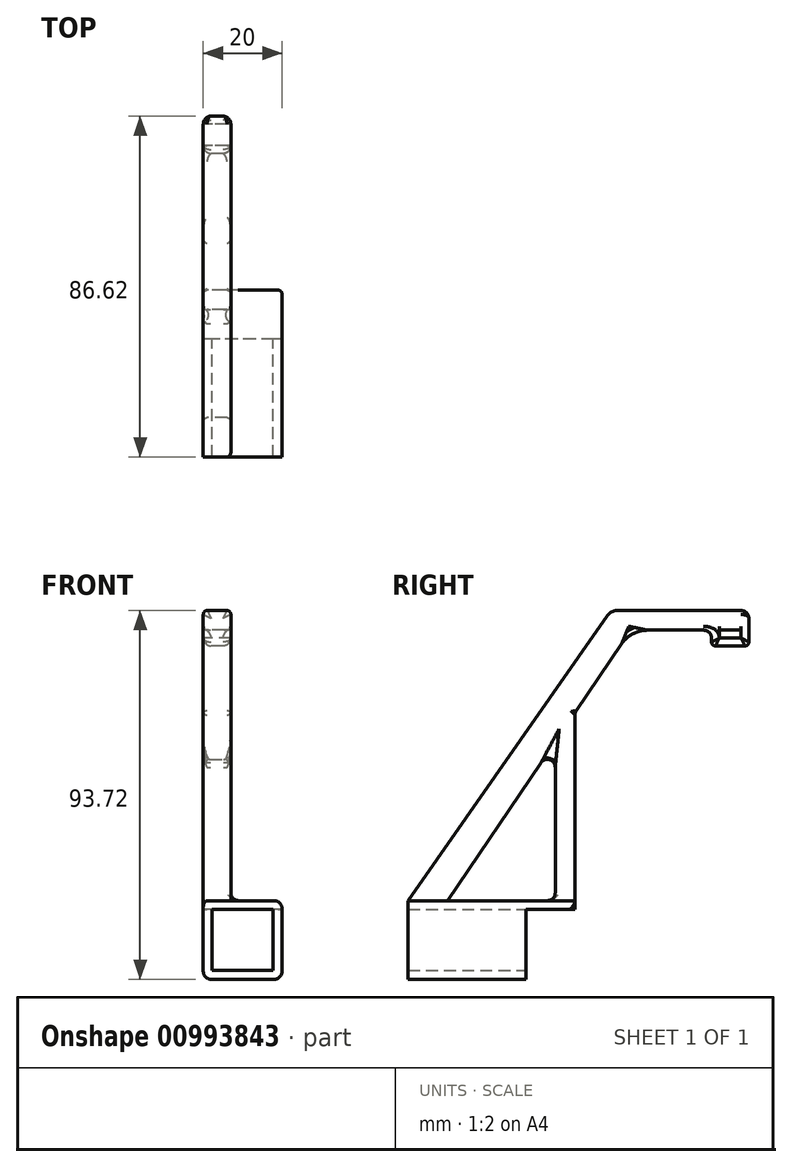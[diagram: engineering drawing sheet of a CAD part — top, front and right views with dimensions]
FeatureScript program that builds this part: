
annotation { "Feature Type Name" : "Feature", "Feature Type Description" : "" }
export const myFeature = defineFeature(function(context is Context, id is Id, definition is map)
    precondition{}
    {
        {
            var Q0;
            Q0=qCreatedBy(makeId("Right.planeOp"),FACE);
            var sketch = newSketch(context, id + "F0", { "sketchPlane" : qUnion([Q0])});
            skLineSegment(sketch, "E0.bottom", {"start": v(-15, 0) * mm, "end": v(15, 0) * mm});
            skLineSegment(sketch, "E0.top", {"start": v(-15, -20) * mm, "end": v(15, -20) * mm});
            skLineSegment(sketch, "E0.left", {"start": v(-15, 0) * mm, "end": v(-15, -20) * mm});
            skLineSegment(sketch, "E0.right", {"start": v(15, 0) * mm, "end": v(15, -20) * mm});
            skLineSegment(sketch, "E1", {"start": v(15, 0) * mm, "end": v(-36.62, 73.72) * mm});
            skLineSegment(sketch, "E2", {"start": v(-36.62, 73.72) * mm, "end": v(-71.62, 73.72) * mm});
            skLineSegment(sketch, "E3", {"start": v(-71.62, 73.72) * mm, "end": v(-71.62, 68.72) * mm});
            skLineSegment(sketch, "E4", {"start": v(-71.62, 68.72) * mm, "end": v(-41.62, 68.72) * mm});
            skLineSegment(sketch, "E5", {"start": v(-41.62, 68.72) * mm, "end": v(5, 0) * mm});
            skLineSegment(sketch, "E6", {"start": v(-15, 0) * mm, "end": v(-27.41, 0) * mm});
            skLineSegment(sketch, "E7", {"start": v(-27.41, 0) * mm, "end": v(-27.41, -2.25) * mm});
            skLineSegment(sketch, "E8", {"start": v(-27.41, -2.25) * mm, "end": v(-15, -2.25) * mm});
            skLineSegment(sketch, "E9", {"start": v(-27.41, 0) * mm, "end": v(-27.41, 47.78) * mm});
            skLineSegment(sketch, "E10", {"start": v(-22.41, 0) * mm, "end": v(-22.41, 40.4) * mm});
            skLineSegment(sketch, "E11", {"start": v(-71.62, 68.72) * mm, "end": v(-71.62, 64.72) * mm});
            skLineSegment(sketch, "E12", {"start": v(-71.62, 64.72) * mm, "end": v(-62.12, 64.72) * mm});
            skLineSegment(sketch, "E13", {"start": v(-62.12, 64.72) * mm, "end": v(-62.12, 68.72) * mm});
            skLineSegment(sketch, "E14", {"start": v(-69.62, 68.72) * mm, "end": v(-69.62, 66.72) * mm});
            skLineSegment(sketch, "E15", {"start": v(-69.62, 66.72) * mm, "end": v(-64.12, 66.72) * mm});
            skLineSegment(sketch, "E16", {"start": v(-64.12, 66.72) * mm, "end": v(-64.12, 68.72) * mm});
            skSolve(sketch);
        }
        {
            var Q0;
            Q0=makeQuery(id+"F0.imprint","IMPRINT",FACE,{"disambiguationData":[TD([[makeQuery(id+"F0.imprint","IMPRINT",EDGE,{"derivedFrom":sQuery(id+"F0.wireOp",EDGE,"E0.top")}),1.0]])]});
            var Q1;
            {var subQ0=sQuery(id+"F0.wireOp",EDGE,"E7");Q1=makeQuery(id+"F0.imprint","IMPRINT",FACE,{"disambiguationData":[TD([[makeQuery(id+"F0.imprint","IMPRINT",EDGE,{"derivedFrom":subQ0}),1.0]])]});}
            extrude(context, id + "F1", {"entities" : qUnion([Q0, Q1]), "depth" : 20 * mm, "offsetDistance" : 25 * mm});
        }
        {
            var Q0;
            {var subQ0=sQuery(id+"F0.wireOp",EDGE,"E1");Q0=makeQuery(id+"F0.imprint","IMPRINT",FACE,{"disambiguationData":[TD([[makeQuery(id+"F0.imprint","IMPRINT",EDGE,{"derivedFrom":subQ0}),1.0]])]});}
            var Q1;
            {var subQ0=sQuery(id+"F0.wireOp",EDGE,"JJyUEpVb-gie7-RlF8-7qWe-H1qUGamomeF3");Q1=makeQuery(id+"F0.imprint","IMPRINT",FACE,{"disambiguationData":[TD([[makeQuery(id+"F0.imprint","IMPRINT",EDGE,{"derivedFrom":subQ0}),-1.0]])]});}
            var Q2;
            {var subQ0=sQuery(id+"F0.wireOp",EDGE,"E9");Q2=makeQuery(id+"F0.imprint","IMPRINT",FACE,{"disambiguationData":[TD([[makeQuery(id+"F0.imprint","IMPRINT",EDGE,{"derivedFrom":subQ0}),-1.0]])]});}
            var Q3;
            {var subQ0=sQuery(id+"F0.wireOp",EDGE,"E11");Q3=makeQuery(id+"F0.imprint","IMPRINT",FACE,{"disambiguationData":[TD([[makeQuery(id+"F0.imprint","IMPRINT",EDGE,{"derivedFrom":subQ0}),1.0]])]});}
            extrude(context, id + "F2", {"entities" : qUnion([Q0, Q1, Q2, Q3]), "operationType" : NewBodyOperationType.ADD, "depth" : 7 * mm, "offsetDistance" : 25 * mm});
        }
        {
            var Q0;
            Q0=makeQuery(id+"F1.opExtrude","SWEPT_FACE",FACE,{"disambiguationData":[OSD([sQuery(id+"F0.wireOp",EDGE,"E0.left")])]});
            var sketch = newSketch(context, id + "F3", { "sketchPlane" : qUnion([Q0])});
            skLineSegment(sketch, "E17.bottom", {"start": v(17.75, -2.25) * mm, "end": v(2.25, -2.25) * mm});
            skLineSegment(sketch, "E17.top", {"start": v(17.75, -17.75) * mm, "end": v(2.25, -17.75) * mm});
            skLineSegment(sketch, "E17.left", {"start": v(17.75, -2.25) * mm, "end": v(17.75, -17.75) * mm});
            skLineSegment(sketch, "E17.right", {"start": v(2.25, -2.25) * mm, "end": v(2.25, -17.75) * mm});
            skPoint(sketch, "E17.middle", {"position": v(0, -10) * mm});
            skSolve(sketch);
        }
        {
            var Q0;
            Q0=makeQuery(id+"F3.imprint","IMPRINT",FACE,{"disambiguationData":[TD([[makeQuery(id+"F3.imprint","IMPRINT",EDGE,{"derivedFrom":sQuery(id+"F3.wireOp",EDGE,"E17.bottom")}),1.0]])]});
            var Q1;
            Q1=makeQuery(id+"F1.opExtrude","SWEPT_FACE",FACE,{"disambiguationData":[OSD([sQuery(id+"F0.wireOp",EDGE,"E0.right")])]});
            extrude(context, id + "F4", {"entities" : qUnion([Q0]), "operationType" : NewBodyOperationType.REMOVE, "endBound" : BoundingType.UP_TO_SURFACE, "oppositeDirection" : true, "depth" : 25 * mm, "endBoundEntityFace" : qUnion([Q1]), "offsetDistance" : 25 * mm});
        }
        {
            var Q0;
            Q0=makeQuery(id+"F2.opExtrude","CAP_EDGE",EDGE,{"disambiguationData":[OSD([sQuery(id+"F0.wireOp",EDGE,"E2")])],"isStart":false});
            var Q1;
            Q1=makeQuery(id+"F2.opExtrude","CAP_EDGE",EDGE,{"disambiguationData":[OSD([sQuery(id+"F0.wireOp",EDGE,"E4")])],"isStart":false});
            var Q2;
            Q2=makeQuery(id+"F2.opExtrude","CAP_EDGE",EDGE,{"disambiguationData":[OSD([sQuery(id+"F0.wireOp",EDGE,"E5")])],"isStart":false});
            var Q3;
            Q3=makeQuery(id+"F2.opExtrude","CAP_EDGE",EDGE,{"disambiguationData":[OSD([sQuery(id+"F0.wireOp",EDGE,"E2")])],"isStart":true});
            var Q4;
            Q4=makeQuery(id+"F2.opExtrude","CAP_EDGE",EDGE,{"disambiguationData":[OSD([sQuery(id+"F0.wireOp",EDGE,"E4")])],"isStart":true});
            var Q5;
            Q5=makeQuery(id+"F2.opExtrude","CAP_EDGE",EDGE,{"disambiguationData":[OSD([sQuery(id+"F0.wireOp",EDGE,"E5")])],"isStart":true});
            var Q6;
            Q6=makeQuery(id+"F2.opExtrude","CAP_EDGE",EDGE,{"disambiguationData":[OSD([sQuery(id+"F0.wireOp",EDGE,"E1")])],"isStart":false});
            var Q7;
            Q7=makeQuery(id+"F2.opExtrude","CAP_EDGE",EDGE,{"disambiguationData":[OSD([sQuery(id+"F0.wireOp",EDGE,"E1")])],"isStart":true});
            var Q8;
            Q8=makeQuery(id+"F2.opExtrude","CAP_EDGE",EDGE,{"disambiguationData":[OSD([sQuery(id+"F0.wireOp",EDGE,"MwvaDB4x-Gc2K-hVEB-6IYb-x19hV3h6sSwj")])],"isStart":false});
            var Q9;
            Q9=makeQuery(id+"F2.opExtrude","CAP_EDGE",EDGE,{"disambiguationData":[OSD([sQuery(id+"F0.wireOp",EDGE,"JJyUEpVb-gie7-RlF8-7qWe-H1qUGamomeF3")])],"isStart":false});
            var Q10;
            Q10=makeQuery(id+"F2.opExtrude","CAP_EDGE",EDGE,{"disambiguationData":[OSD([sQuery(id+"F0.wireOp",EDGE,"MwvaDB4x-Gc2K-hVEB-6IYb-x19hV3h6sSwj")])],"isStart":true});
            var Q11;
            Q11=makeQuery(id+"F2.boolean.opBoolean","MERGE",EDGE,{"derivedFrom":[makeQuery(id+"F1.opExtrude","CAP_EDGE",EDGE,{"disambiguationData":[OSD([sQuery(id+"F0.wireOp",EDGE,"E0.left")])],"isStart":true}),makeQuery(id+"F2.opExtrude","CAP_EDGE",EDGE,{"disambiguationData":[OSD([sQuery(id+"F0.wireOp",EDGE,"JJyUEpVb-gie7-RlF8-7qWe-H1qUGamomeF3")])],"isStart":true})]});
            var Q12;
            Q12=makeQuery(id+"F2.opExtrude","CAP_EDGE",EDGE,{"disambiguationData":[OSD([sQuery(id+"F0.wireOp",EDGE,"E9")])],"isStart":false});
            var Q13;
            Q13=makeQuery(id+"F2.opExtrude","CAP_EDGE",EDGE,{"disambiguationData":[OSD([sQuery(id+"F0.wireOp",EDGE,"E10")])],"isStart":false});
            var Q14;
            Q14=makeQuery(id+"F2.boolean.opBoolean","MERGE",EDGE,{"derivedFrom":[makeQuery(id+"F1.opExtrude","CAP_EDGE",EDGE,{"disambiguationData":[OSD([sQuery(id+"F0.wireOp",EDGE,"E7")])],"isStart":true}),makeQuery(id+"F2.opExtrude","CAP_EDGE",EDGE,{"disambiguationData":[OSD([sQuery(id+"F0.wireOp",EDGE,"E9")])],"isStart":true})]});
            var Q15;
            Q15=makeQuery(id+"F2.opExtrude","CAP_EDGE",EDGE,{"disambiguationData":[OSD([sQuery(id+"F0.wireOp",EDGE,"E10")])],"isStart":true});
            var Q16;
            Q16=makeQuery(id+"F1.opExtrude","CAP_EDGE",EDGE,{"disambiguationData":[OSD([sQuery(id+"F0.wireOp",EDGE,"E7")])],"isStart":false});
            var Q17;
            Q17=makeQuery(id+"F2.opExtrude","SWEPT_EDGE",EDGE,{"disambiguationData":[OSD([sQuery(id+"F0.wireOp",EDGE,"E11"),sQuery(id+"F0.wireOp",EDGE,"E12")])]});
            var Q18;
            Q18=makeQuery(id+"F2.opExtrude","SWEPT_EDGE",EDGE,{"disambiguationData":[OSD([sQuery(id+"F0.wireOp",EDGE,"E12"),sQuery(id+"F0.wireOp",EDGE,"E13")])]});
            fillet(context, id + "F5", {"entities" : qUnion([Q0, Q1, Q2, Q3, Q4, Q5, Q6, Q7, Q8, Q9, Q10, Q11, Q12, Q13, Q14, Q15, Q16, Q17, Q18]), "tangentPropagation" : true, "radius" : 1 * mm, "defaultsChanged" : true, "vertexSettings" : [], "allowEdgeOverflow" : false});
        }
        {
            var Q0;
            Q0=makeQuery(id+"F2.opExtrude","CAP_EDGE",EDGE,{"disambiguationData":[OSD([sQuery(id+"F0.wireOp",EDGE,"E0.bottom")])],"isStart":false});
            var Q1;
            Q1=makeQuery(id+"F5.opFillet","BLEND_EDGE",EDGE,{"blendedFrom":[makeQuery(id+"F2.opExtrude","CAP_EDGE",EDGE,{"disambiguationData":[OSD([sQuery(id+"F0.wireOp",EDGE,"E4")])],"isStart":true}),makeQuery(id+"F2.opExtrude","CAP_EDGE",EDGE,{"disambiguationData":[OSD([sQuery(id+"F0.wireOp",EDGE,"E5")])],"isStart":true})],"blendedInto":[]});
            fillet(context, id + "F6", {"entities" : qUnion([Q0, Q1]), "tangentPropagation" : true, "radius" : 8 * mm, "defaultsChanged" : true, "vertexSettings" : [], "allowEdgeOverflow" : false});
        }
        {
            var Q0;
            Q0=makeQuery(id+"F5.opFillet","BLEND_EDGE",EDGE,{"blendedFrom":[makeQuery(id+"F2.opExtrude","CAP_EDGE",EDGE,{"disambiguationData":[OSD([sQuery(id+"F0.wireOp",EDGE,"E1")])],"isStart":true}),makeQuery(id+"F2.opExtrude","CAP_EDGE",EDGE,{"disambiguationData":[OSD([sQuery(id+"F0.wireOp",EDGE,"E2")])],"isStart":true})],"blendedInto":[]});
            fillet(context, id + "F7", {"entities" : qUnion([Q0]), "tangentPropagation" : true, "radius" : 3 * mm, "defaultsChanged" : false, "vertexSettings" : [], "allowEdgeOverflow" : false});
        }
        {
            var Q0;
            Q0=makeQuery(id+"F1.opExtrude","CAP_EDGE",EDGE,{"disambiguationData":[OSD([sQuery(id+"F0.wireOp",EDGE,"E0.top")])],"isStart":true});
            var Q1;
            Q1=makeQuery(id+"F1.opExtrude","CAP_EDGE",EDGE,{"disambiguationData":[OSD([sQuery(id+"F0.wireOp",EDGE,"E0.top")])],"isStart":false});
            var Q2;
            Q2=makeQuery(id+"F1.opExtrude","CAP_EDGE",EDGE,{"disambiguationData":[OSD([sQuery(id+"F0.wireOp",EDGE,"E0.bottom")])],"isStart":false});
            fillet(context, id + "F8", {"entities" : qUnion([Q0, Q1, Q2]), "radius" : 2 * mm, "defaultsChanged" : true, "vertexSettings" : [], "allowEdgeOverflow" : false});
        }
        {
            var Q0;
            Q0=makeQuery(id+"F5.opFillet","BLEND_EDGE",EDGE,{"blendedFrom":[makeQuery(id+"F2.opExtrude","CAP_EDGE",EDGE,{"disambiguationData":[OSD([sQuery(id+"F0.wireOp",EDGE,"E9")])],"isStart":false}),makeQuery(id+"F1.opExtrude","SWEPT_FACE",FACE,{"disambiguationData":[OSD([sQuery(id+"F0.wireOp",EDGE,"E0.bottom"),sQuery(id+"F0.wireOp",EDGE,"E6")])]})],"blendedInto":[makeQuery(id+"F1.opExtrude","SWEPT_FACE",FACE,{"disambiguationData":[OSD([sQuery(id+"F0.wireOp",EDGE,"E0.bottom"),sQuery(id+"F0.wireOp",EDGE,"E6")])]})]});
            var Q1;
            {var subQ0=sQuery(id+"F0.wireOp",EDGE,"E10");var subQ1=sQuery(id+"F0.wireOp",EDGE,"E5");Q1=makeQuery(id+"F5.opFillet","BLEND_EDGE",EDGE,{"blendedFrom":[makeQuery(id+"F2.opExtrude","CAP_EDGE",EDGE,{"disambiguationData":[OSD([subQ1]),TDD([makeQuery(id+"F0.imprint","IMPRINT",EDGE,{"disambiguationData":[TD([[makeQuery(id+"F0.imprint","INTERSECT",VERTEX,{"derivedFrom":[sQuery(id+"F0.wireOp",EDGE,"E0.bottom"),subQ1]}),1.0]])],"derivedFrom":subQ1})])],"isStart":false}),makeQuery(id+"F2.opExtrude","CAP_EDGE",EDGE,{"disambiguationData":[OSD([subQ0])],"isStart":false})],"blendedInto":[]});}
            var Q2;
            {var subQ0=sQuery(id+"F0.wireOp",EDGE,"E9");var subQ1=sQuery(id+"F0.wireOp",EDGE,"E5");Q2=makeQuery(id+"F5.opFillet","BLEND_EDGE",EDGE,{"blendedFrom":[makeQuery(id+"F2.opExtrude","CAP_EDGE",EDGE,{"disambiguationData":[OSD([subQ1]),TDD([makeQuery(id+"F0.imprint","IMPRINT",EDGE,{"disambiguationData":[TD([[makeQuery(id+"F0.imprint","INTERSECT",VERTEX,{"derivedFrom":[sQuery(id+"F0.wireOp",EDGE,"E4"),subQ1]}),-1.0]])],"derivedFrom":subQ1})])],"isStart":false}),makeQuery(id+"F2.opExtrude","CAP_EDGE",EDGE,{"disambiguationData":[OSD([subQ0])],"isStart":false})],"blendedInto":[]});}
            var Q3;
            Q3=makeQuery(id+"F5.opFillet","BLEND_EDGE",EDGE,{"blendedFrom":[makeQuery(id+"F2.opExtrude","CAP_EDGE",EDGE,{"disambiguationData":[OSD([sQuery(id+"F0.wireOp",EDGE,"E2")])],"isStart":false}),makeQuery(id+"F2.opExtrude","SWEPT_FACE",FACE,{"disambiguationData":[OSD([sQuery(id+"F0.wireOp",EDGE,"E3"),sQuery(id+"F0.wireOp",EDGE,"E11")])]})],"blendedInto":[makeQuery(id+"F2.opExtrude","SWEPT_FACE",FACE,{"disambiguationData":[OSD([sQuery(id+"F0.wireOp",EDGE,"E3"),sQuery(id+"F0.wireOp",EDGE,"E11")])]})]});
            var Q4;
            Q4=makeQuery(id+"F2.opExtrude","SWEPT_EDGE",EDGE,{"disambiguationData":[OSD([sQuery(id+"F0.wireOp",EDGE,"E4"),sQuery(id+"F0.wireOp",EDGE,"E13")])]});
            fillet(context, id + "F9", {"entities" : qUnion([Q0, Q1, Q2, Q3, Q4]), "tangentPropagation" : true, "radius" : 2 * mm, "defaultsChanged" : false, "vertexSettings" : [], "allowEdgeOverflow" : false});
        }
        {
            var Q0;
            Q0=makeQuery(id+"F1.opExtrude","SWEPT_BODY",BODY,{"disambiguationData":[OSD([sQuery(id+"F0.wireOp",EDGE,"E0.bottom"),sQuery(id+"F0.wireOp",EDGE,"E0.top"),sQuery(id+"F0.wireOp",EDGE,"E0.left"),sQuery(id+"F0.wireOp",EDGE,"E0.right"),sQuery(id+"F0.wireOp",EDGE,"E6"),sQuery(id+"F0.wireOp",EDGE,"E7"),sQuery(id+"F0.wireOp",EDGE,"E8")])]});
            transform(context, id + "F10", {"entities" : qUnion([Q0]), "transformType" : TransformType.TRANSLATION_3D, "dx" : 0 * mm, "dy" : -50 * mm, "dz" : 0 * mm, "makeCopy" : false});
        }
        {
            var Q0;
            Q0=makeQuery(id+"F1.opExtrude","SWEPT_BODY",BODY,{"disambiguationData":[OSD([sQuery(id+"F0.wireOp",EDGE,"E0.bottom"),sQuery(id+"F0.wireOp",EDGE,"E0.top"),sQuery(id+"F0.wireOp",EDGE,"E0.left"),sQuery(id+"F0.wireOp",EDGE,"E0.right"),sQuery(id+"F0.wireOp",EDGE,"E6"),sQuery(id+"F0.wireOp",EDGE,"E7"),sQuery(id+"F0.wireOp",EDGE,"E8")])]});
            var Q1;
            Q1=qCreatedBy(makeId("Front.planeOp"),FACE);
            mirror(context, id + "F11", {"entities" : qUnion([Q0]), "mirrorPlane" : qUnion([Q1])});
        }
        {
            var Q0;
            Q0=makeQuery(id+"F1.opExtrude","SWEPT_BODY",BODY,{"disambiguationData":[OSD([sQuery(id+"F0.wireOp",EDGE,"E0.bottom"),sQuery(id+"F0.wireOp",EDGE,"E0.top"),sQuery(id+"F0.wireOp",EDGE,"E0.left"),sQuery(id+"F0.wireOp",EDGE,"E0.right"),sQuery(id+"F0.wireOp",EDGE,"E6"),sQuery(id+"F0.wireOp",EDGE,"E7"),sQuery(id+"F0.wireOp",EDGE,"E8")])]});
            deleteBodies(context, id + "F12", {"entities" : qUnion([Q0])});
        }
    });
